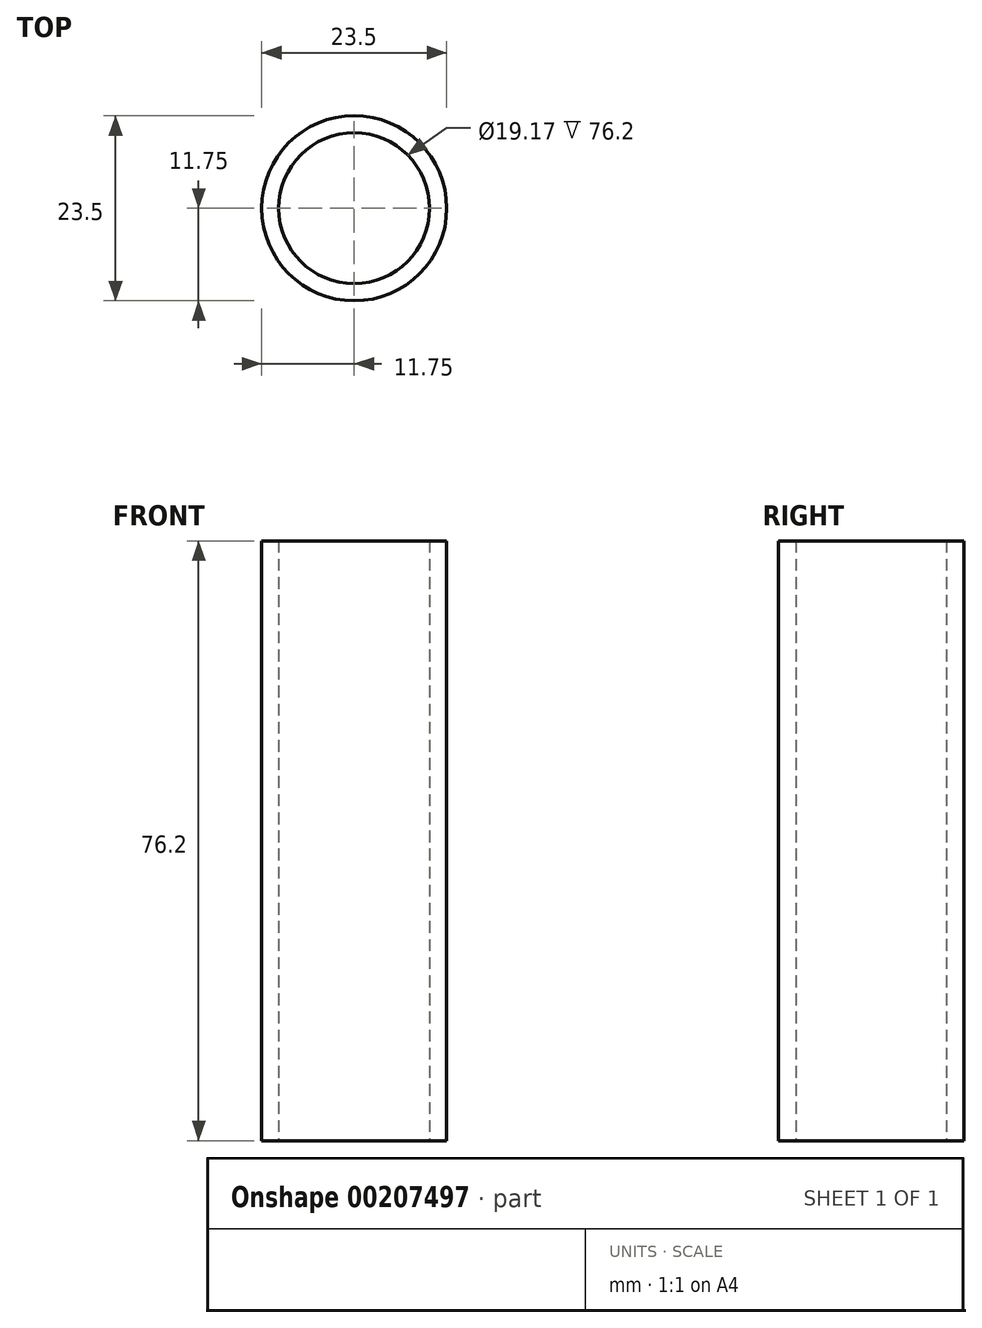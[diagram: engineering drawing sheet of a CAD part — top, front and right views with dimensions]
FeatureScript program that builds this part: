
annotation { "Feature Type Name" : "Feature", "Feature Type Description" : "" }
export const myFeature = defineFeature(function(context is Context, id is Id, definition is map)
    precondition{}
    {
        {
            var Q0;
            Q0=qCreatedBy(makeId("Top.planeOp"),FACE);
            var sketch = newSketch(context, id + "F0", { "sketchPlane" : qUnion([Q0])});
            skCircle(sketch, "E0", {"center": v(0, 0) * mm, "radius": 11.75 * mm});
            skSolve(sketch);
        }
        {
            var Q0;
            Q0 = qSketchRegion(id + "F0", true);
            extrude(context, id + "F1", {"entities" : qUnion([Q0]), "endBound" : BoundingType.SYMMETRIC, "depth" : 76.2 * mm});
        }
        {
            var Q0;
            Q0=qCreatedBy(makeId("Top.planeOp"),FACE);
            var sketch = newSketch(context, id + "F2", { "sketchPlane" : qUnion([Q0])});
            skCircle(sketch, "E1", {"center": v(0, 0) * mm, "radius": 9.59 * mm});
            skSolve(sketch);
        }
        {
            var Q0;
            Q0 = qSketchRegion(id + "F2", true);
            extrude(context, id + "F3", {"entities" : qUnion([Q0]), "operationType" : NewBodyOperationType.REMOVE, "endBound" : BoundingType.SYMMETRIC, "depth" : 76.2 * mm});
        }
    });
